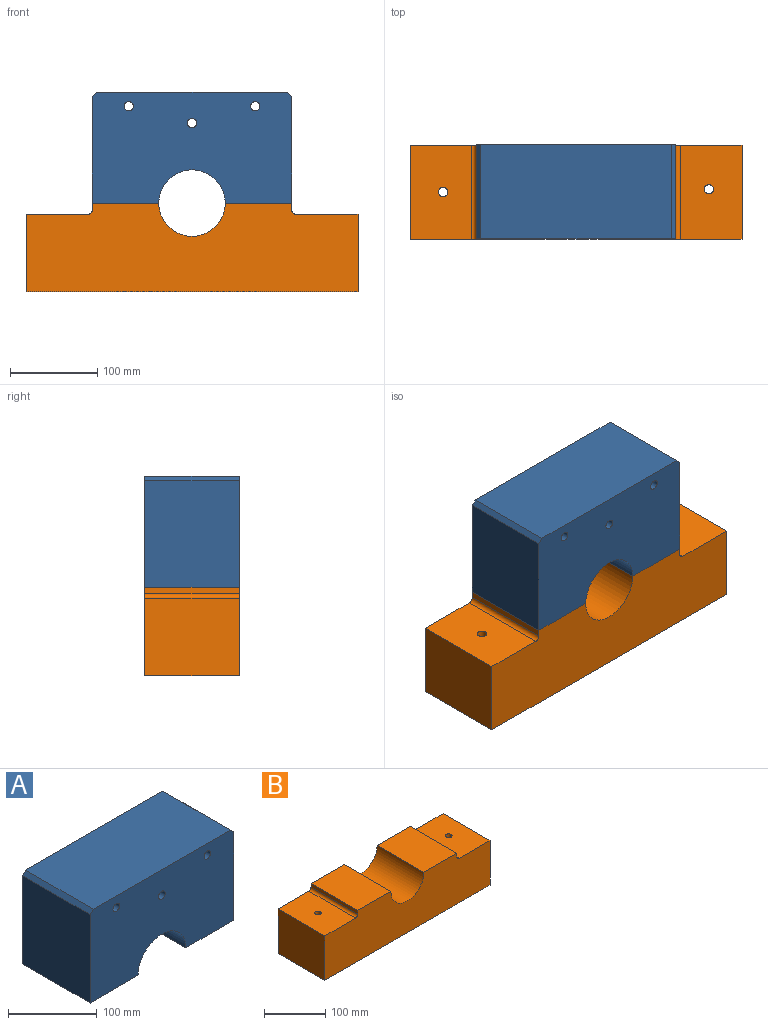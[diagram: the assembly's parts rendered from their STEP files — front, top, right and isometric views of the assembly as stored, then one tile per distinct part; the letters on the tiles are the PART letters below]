
ASSEMBLY  parts=2 mates=1
PART A: 13 faces, bbox 228.6x108x127 mm
  f0: plane 121.92x107.95mm, normal (-1,0,0), area 13161.3mm2, adj f5,f6,f7,f12
  f1: plane 218.44x107.95mm, normal (0,0,1), area 23580.6mm2, adj f6,f7,f11,f12
  f2: plane 121.92x107.95mm, normal (1,0,0), area 13161.3mm2, adj f3,f6,f7,f11
  f3: plane 107.95x76.2mm, normal (0,0,-1), area 8225.8mm2, adj f2,f4,f6,f7
  f4: cylinder r=38.1mm len=107.95mm, axis (0,-1,0), area 12921mm2, adj f3,f5,f6,f7
  f5: plane 107.95x76.2mm, normal (0,0,-1), area 8225.8mm2, adj f0,f4,f6,f7
  f6: plane 228.6x127mm, normal (0,1,0), area 26455.6mm2, adj f0,f1,f2,f3,f4,f5,f8,f9
  f7: plane 228.6x127mm, normal (0,-1,0), area 26455.6mm2, adj f0,f1,f2,f3,f4,f5,f8,f9
  f8: cylinder r=5.36mm len=107.95mm, axis (0,-1,0), area 3634.3mm2, adj f6,f7
  f9: cylinder r=5.36mm len=107.95mm, axis (0,-1,0), area 3634.3mm2, adj f6,f7
  f10: cylinder r=5.36mm len=107.95mm, axis (0,-1,0), area 3634.3mm2, adj f6,f7
  f11: plane 107.95x5.08mm, normal (0.71,0,0.71), area 775.5mm2, adj f1,f2,f6,f7
  f12: plane 107.95x5.08mm, normal (-0.71,0,0.71), area 775.5mm2, adj f0,f1,f6,f7
PART B: 16 faces, bbox 381x108x101.6 mm
  f0: plane 107.95x71.12mm, normal (0,0,1), area 7587.2mm2, adj f1,f10,f11,f13,f15
  f1: plane 107.95x88.9mm, normal (1,0,0), area 9596.8mm2, adj f0,f2,f10,f11
  f2: plane 381x107.95mm, normal (0,0,-1), area 40948.6mm2, adj f1,f3,f10,f11,f12,f13
  f3: plane 107.95x88.9mm, normal (-1,0,0), area 9596.8mm2, adj f2,f4,f10,f11
  f4: plane 107.95x71.12mm, normal (0,0,1), area 7587.2mm2, adj f3,f10,f11,f12,f14
  f5: plane 107.95x7.62mm, normal (-1,0,0), area 822.6mm2, adj f6,f10,f11,f14
  f6: plane 107.95x76.2mm, normal (0,0,1), area 8225.8mm2, adj f5,f7,f10,f11
  f7: cylinder r=38.1mm len=107.95mm, axis (0,-1,0), area 12921mm2, adj f6,f8,f10,f11
  f8: plane 107.95x76.2mm, normal (0,0,1), area 8225.8mm2, adj f7,f9,f10,f11
  f9: plane 107.95x7.62mm, normal (1,0,0), area 822.6mm2, adj f8,f10,f11,f15
  f10: plane 381x101.6mm, normal (0,1,0), area 34505mm2, adj f0,f1,f2,f3,f4,f5,f6,f7
  f11: plane 381x101.6mm, normal (0,-1,0), area 34505mm2, adj f0,f1,f2,f3,f4,f5,f6,f7
  f12: cylinder r=5.36mm len=88.9mm, axis (0,0,1), area 2992.9mm2, adj f2,f4
  f13: cylinder r=5.36mm len=88.9mm, axis (0,0,1), area 2992.9mm2, adj f0,f2
  f14: cylinder r=5.08mm len=107.95mm, axis (0,1,0), area 861.4mm2, adj f4,f5,f10,f11
  f15: cylinder r=5.08mm len=107.95mm, axis (0,-1,0), area 861.4mm2, adj f0,f9,f10,f11
PLACE A t=(-88.9,-53.97,177.39)mm
PLACE B t=(-88.9,-53.97,177.39)mm
MATE fastened A.f3 <-> B.f8  axis (0,0,-1) through (76.2,0.01,101.6)mm
